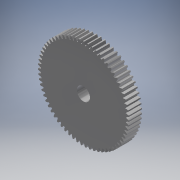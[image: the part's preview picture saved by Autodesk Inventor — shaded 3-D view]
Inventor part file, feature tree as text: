
AUTODESK INVENTOR PART (.ipt)
format: ipt  version: 2017 (Build 210142000, 142)  size: 429,056 bytes
history: native  units: mm (DEFAULTED — no unit token found)
features: plane x3, other x3, sketch x3, extrude x2
ambient origin geometry x8: Origin, YZ Plane, XZ Plane, XY Plane, X Axis, Y Axis, Z Axis, Center Point
bodies: Solid1 (feature_tree)
feature tree (11):
  extrude  "Extrusion1"  Depth=25.4mm TaperAngle=0.0deg
  plane  "Work Plane1"
  plane  "Work Plane2"
  plane  "Work Plane3"
  other  "Spur Gear"
  extrude  "Extrusion2"  Depth=76.2mm TaperAngle=0.0deg
  sketch  "Sketch1"  dims[d0=175.26mm d1=25.4mm d2=0.0mm]
  sketch  "Sketch2"  dims[d3=170.18mm d4=76.2mm d5=0.0mm]
  other  "Srf1"
  sketch  "Sketch3"  dims[d6=0.0mm d7=0.468894mm d9=0.0mm d14=0.0mm d15=101.6mm d16=0.0mm d17=0.0mm d18=0.0mm d19=101.6mm d20=25.4mm d21=25.4mm d22=0.0mm]
  other  "Pitch Diameter"
